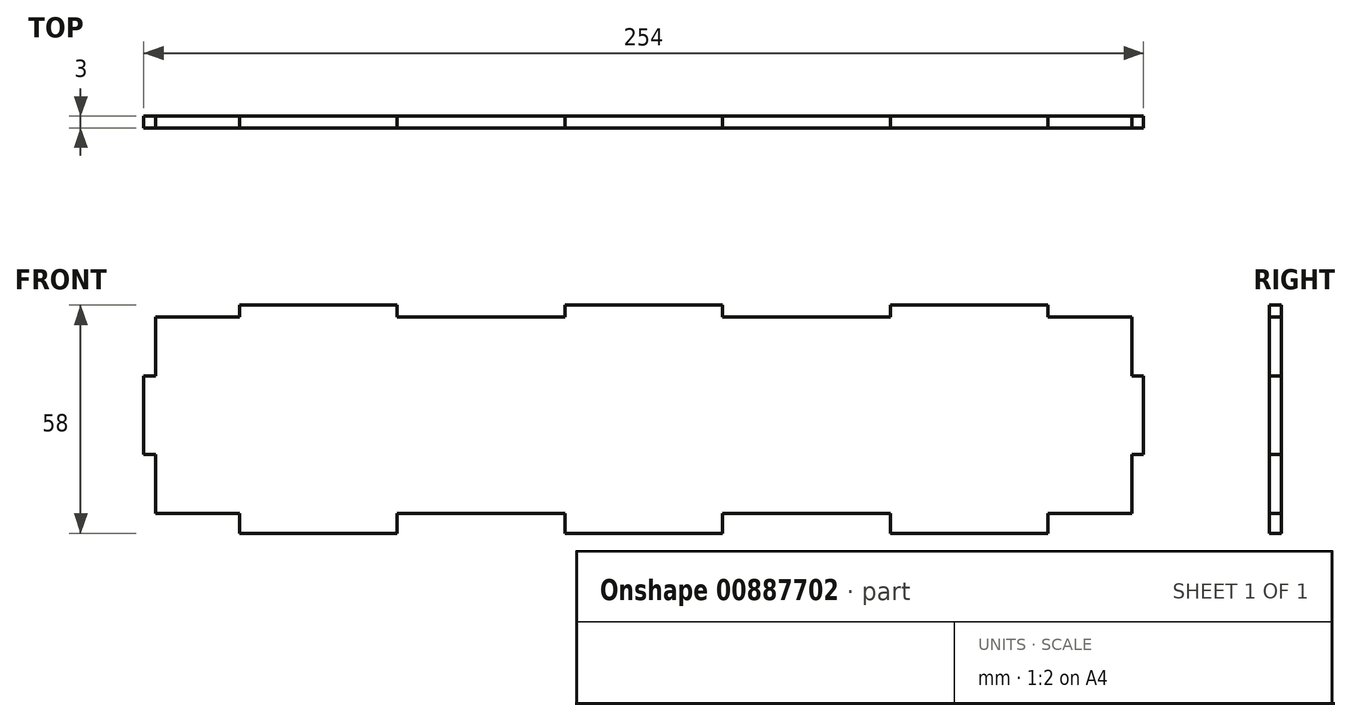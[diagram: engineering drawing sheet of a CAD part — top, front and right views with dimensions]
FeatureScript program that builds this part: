
annotation { "Feature Type Name" : "Feature", "Feature Type Description" : "" }
export const myFeature = defineFeature(function(context is Context, id is Id, definition is map)
    precondition{}
    {
        {
            var Q0;
            Q0=qCreatedBy(makeId("Front.planeOp"),FACE);
            var sketch = newSketch(context, id + "F0", { "sketchPlane" : qUnion([Q0])});
            skLineSegment(sketch, "E0.bottom", {"start": v(124, -25) * mm, "end": v(102.67, -25) * mm});
            skLineSegment(sketch, "E0.top", {"start": v(124, 25) * mm, "end": v(102.67, 25) * mm});
            skLineSegment(sketch, "E0.left", {"start": v(124, -25) * mm, "end": v(124, -10) * mm});
            skLineSegment(sketch, "E0.right", {"start": v(-124, -25) * mm, "end": v(-124, -10) * mm});
            skPoint(sketch, "E0.middle", {"position": v(0, 0) * mm});
            skLineSegment(sketch, "E1", {"start": v(-102.67, -25) * mm, "end": v(-102.67, -30) * mm});
            skLineSegment(sketch, "E2", {"start": v(-102.67, -30) * mm, "end": v(-62.67, -30) * mm});
            skLineSegment(sketch, "E3", {"start": v(-62.67, -30) * mm, "end": v(-62.67, -25) * mm});
            skLineSegment(sketch, "E4", {"start": v(-20, -25) * mm, "end": v(-20, -30) * mm});
            skLineSegment(sketch, "E5", {"start": v(-20, -30) * mm, "end": v(20, -30) * mm});
            skLineSegment(sketch, "E6", {"start": v(20, -30) * mm, "end": v(20, -25) * mm});
            skLineSegment(sketch, "E7", {"start": v(62.67, -25) * mm, "end": v(62.67, -30) * mm});
            skLineSegment(sketch, "E8", {"start": v(62.67, -30) * mm, "end": v(102.67, -30) * mm});
            skLineSegment(sketch, "E9", {"start": v(102.67, -30) * mm, "end": v(102.67, -25) * mm});
            skLineSegment(sketch, "E10.trimOffspring", {"start": v(-102.67, -25) * mm, "end": v(-124, -25) * mm});
            skLineSegment(sketch, "E11.trimOffspring", {"start": v(-20, -25) * mm, "end": v(-62.67, -25) * mm});
            skLineSegment(sketch, "E12.trimOffspring", {"start": v(62.67, -25) * mm, "end": v(20, -25) * mm});
            skLineSegment(sketch, "E13.MirrorCS", {"start": v(-102.67, 25) * mm, "end": v(-102.67, 28) * mm});
            skLineSegment(sketch, "E14.MirrorCS", {"start": v(-62.67, 28) * mm, "end": v(-62.67, 25) * mm});
            skLineSegment(sketch, "E15.MirrorCS", {"start": v(-20, 25) * mm, "end": v(-20, 28) * mm});
            skLineSegment(sketch, "E16.MirrorCS", {"start": v(20, 28) * mm, "end": v(20, 25) * mm});
            skLineSegment(sketch, "E17.MirrorCS", {"start": v(62.67, 25) * mm, "end": v(62.67, 28) * mm});
            skLineSegment(sketch, "E18.MirrorCS", {"start": v(102.67, 28) * mm, "end": v(102.67, 25) * mm});
            skLineSegment(sketch, "E19.trimOffspring", {"start": v(-102.67, 25) * mm, "end": v(-124, 25) * mm});
            skLineSegment(sketch, "E20.trimOffspring", {"start": v(-20, 25) * mm, "end": v(-62.67, 25) * mm});
            skLineSegment(sketch, "E21.trimOffspring", {"start": v(62.67, 25) * mm, "end": v(20, 25) * mm});
            skLineSegment(sketch, "E22", {"start": v(124, 10) * mm, "end": v(127, 10) * mm});
            skLineSegment(sketch, "E23", {"start": v(127, 10) * mm, "end": v(127, -10) * mm});
            skLineSegment(sketch, "E24", {"start": v(127, -10) * mm, "end": v(124, -10) * mm});
            skLineSegment(sketch, "E25.trimOffspring", {"start": v(124, 10) * mm, "end": v(124, 25) * mm});
            skLineSegment(sketch, "E26.MirrorCS", {"start": v(-124, 10) * mm, "end": v(-127, 10) * mm});
            skLineSegment(sketch, "E27.MirrorCS", {"start": v(-127, 10) * mm, "end": v(-127, -10) * mm});
            skLineSegment(sketch, "E28.MirrorCS", {"start": v(-127, -10) * mm, "end": v(-124, -10) * mm});
            skLineSegment(sketch, "E29.trimOffspring", {"start": v(-124, 10) * mm, "end": v(-124, 25) * mm});
            skLineSegment(sketch, "E30", {"start": v(-102.67, 28) * mm, "end": v(-62.67, 28) * mm});
            skLineSegment(sketch, "E31.MirrorCS", {"start": v(102.67, 28) * mm, "end": v(62.67, 28) * mm});
            skPoint(sketch, "E32.MirrorCS.end.orphan", {"position": v(102.67, 30) * mm});
            skLineSegment(sketch, "E33", {"start": v(-20, 28) * mm, "end": v(20, 28) * mm});
            skSolve(sketch);
        }
        {
            var Q0;
            Q0 = qSketchRegion(id + "F0", true);
            extrude(context, id + "F1", {"entities" : qUnion([Q0]), "depth" : 3 * mm, "offsetDistance" : 25 * mm});
        }
    });
